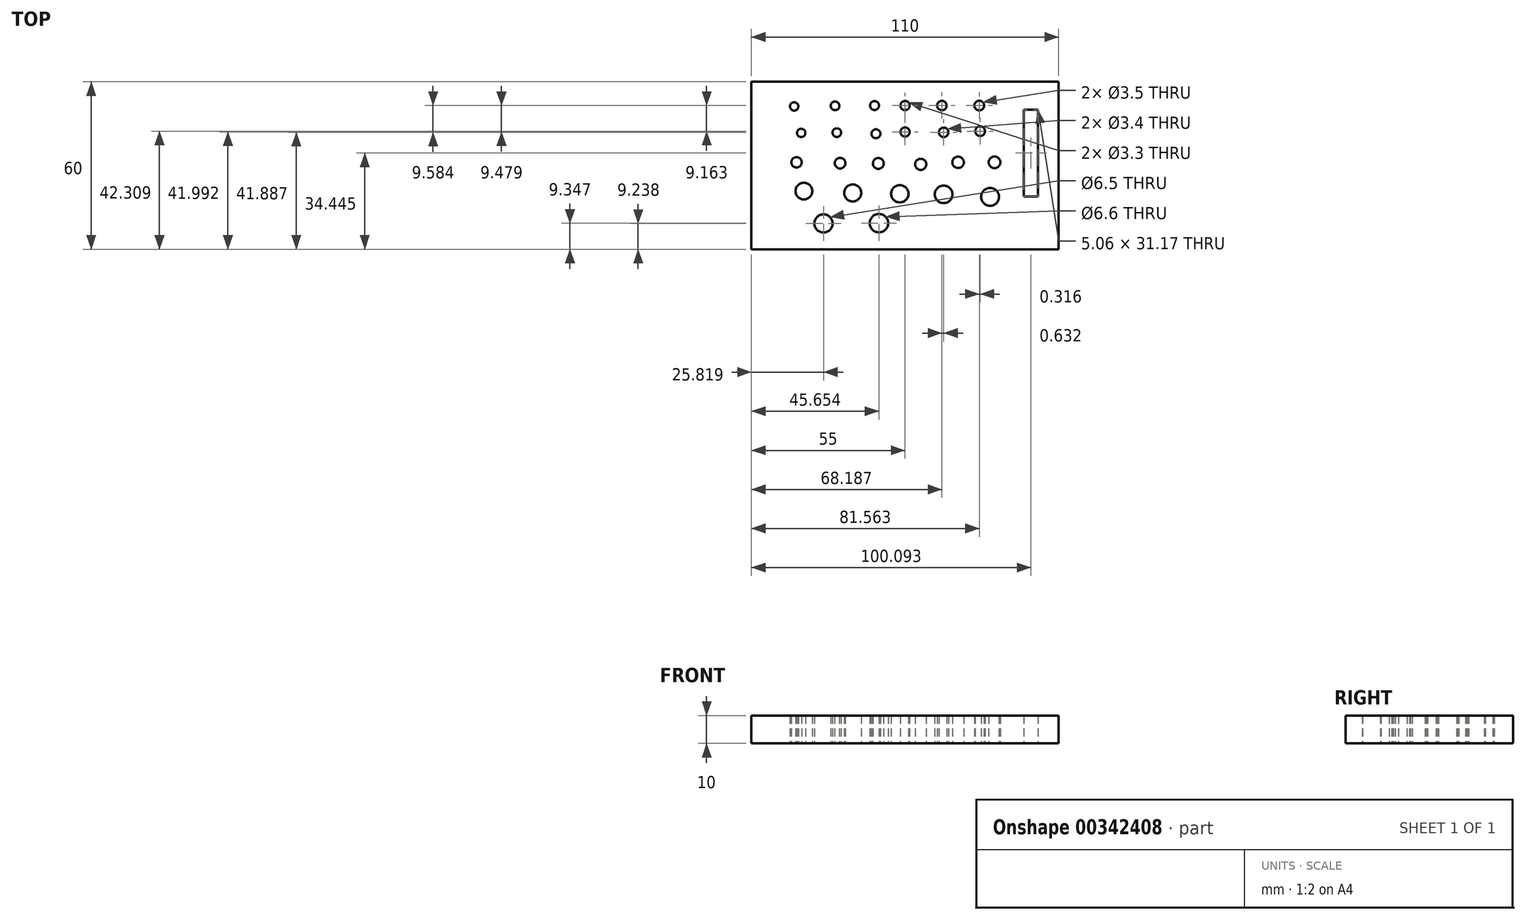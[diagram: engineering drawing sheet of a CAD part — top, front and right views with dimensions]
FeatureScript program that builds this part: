
annotation { "Feature Type Name" : "Feature", "Feature Type Description" : "" }
export const myFeature = defineFeature(function(context is Context, id is Id, definition is map)
    precondition{}
    {
        {
            var Q0;
            Q0=qCreatedBy(makeId("Top.planeOp"),FACE);
            var sketch = newSketch(context, id + "F0", { "sketchPlane" : qUnion([Q0])});
            skLineSegment(sketch, "E0.bottom", {"start": v(55, 30) * mm, "end": v(-55, 30) * mm});
            skLineSegment(sketch, "E0.top", {"start": v(55, -30) * mm, "end": v(-55, -30) * mm});
            skLineSegment(sketch, "E0.left", {"start": v(55, 30) * mm, "end": v(55, -30) * mm});
            skLineSegment(sketch, "E0.right", {"start": v(-55, 30) * mm, "end": v(-55, -30) * mm});
            skPoint(sketch, "E0.middle", {"position": v(0, 0) * mm});
            skCircle(sketch, "E1", {"center": v(-39.68, 21.16) * mm, "radius": 1.5 * mm});
            skCircle(sketch, "E2", {"center": v(-25.04, 21.37) * mm, "radius": 1.55 * mm});
            skCircle(sketch, "E3", {"center": v(-10.93, 21.47) * mm, "radius": 1.6 * mm});
            skCircle(sketch, "E4", {"center": v(0, 21.47) * mm, "radius": 1.65 * mm});
            skCircle(sketch, "E5", {"center": v(13.19, 21.47) * mm, "radius": 1.7 * mm});
            skCircle(sketch, "E6", {"center": v(26.56, 21.47) * mm, "radius": 1.75 * mm});
            skLineSegment(sketch, "E7.bottom", {"start": v(42.57, 20.03) * mm, "end": v(47.62, 20.03) * mm});
            skLineSegment(sketch, "E7.top", {"start": v(42.57, -11.14) * mm, "end": v(47.62, -11.14) * mm});
            skLineSegment(sketch, "E7.left", {"start": v(42.57, 20.03) * mm, "end": v(42.57, -11.14) * mm});
            skLineSegment(sketch, "E7.right", {"start": v(47.62, 20.03) * mm, "end": v(47.62, -11.14) * mm});
            skCircle(sketch, "E8", {"center": v(-37.16, 11.68) * mm, "radius": 1.5 * mm});
            skCircle(sketch, "E9", {"center": v(-24.41, 11.78) * mm, "radius": 1.55 * mm});
            skCircle(sketch, "E10", {"center": v(-10.4, 11.36) * mm, "radius": 1.6 * mm});
            skCircle(sketch, "E11", {"center": v(0, 12) * mm, "radius": 1.65 * mm});
            skCircle(sketch, "E12", {"center": v(13.82, 11.89) * mm, "radius": 1.7 * mm});
            skCircle(sketch, "E13", {"center": v(26.88, 12.3) * mm, "radius": 1.75 * mm});
            skCircle(sketch, "E14", {"center": v(-38.84, 1.14) * mm, "radius": 1.85 * mm});
            skCircle(sketch, "E15", {"center": v(-23.25, 0.83) * mm, "radius": 1.9 * mm});
            skCircle(sketch, "E16", {"center": v(-9.56, 0.72) * mm, "radius": 1.95 * mm});
            skCircle(sketch, "E17", {"center": v(5.6, 0.4) * mm, "radius": 2 * mm});
            skCircle(sketch, "E18", {"center": v(18.98, 1.14) * mm, "radius": 2.05 * mm});
            skCircle(sketch, "E19", {"center": v(32.04, 1.14) * mm, "radius": 2.1 * mm});
            skCircle(sketch, "E20", {"center": v(-36.2, -9.18) * mm, "radius": 3 * mm});
            skCircle(sketch, "E21", {"center": v(-18.72, -9.8) * mm, "radius": 3.05 * mm});
            skCircle(sketch, "E22", {"center": v(-1.87, -10.12) * mm, "radius": 3.1 * mm});
            skCircle(sketch, "E23", {"center": v(13.82, -10.34) * mm, "radius": 3.15 * mm});
            skCircle(sketch, "E24", {"center": v(30.46, -11.23) * mm, "radius": 3.2 * mm});
            skCircle(sketch, "E25", {"center": v(-29.18, -20.76) * mm, "radius": 3.25 * mm});
            skCircle(sketch, "E26", {"center": v(-9.35, -20.65) * mm, "radius": 3.3 * mm});
            skSolve(sketch);
        }
        {
            var Q0;
            Q0 = qSketchRegion(id + "F0", true);
            extrude(context, id + "F1", {"entities" : qUnion([Q0]), "depth" : 10 * mm});
        }
    });
